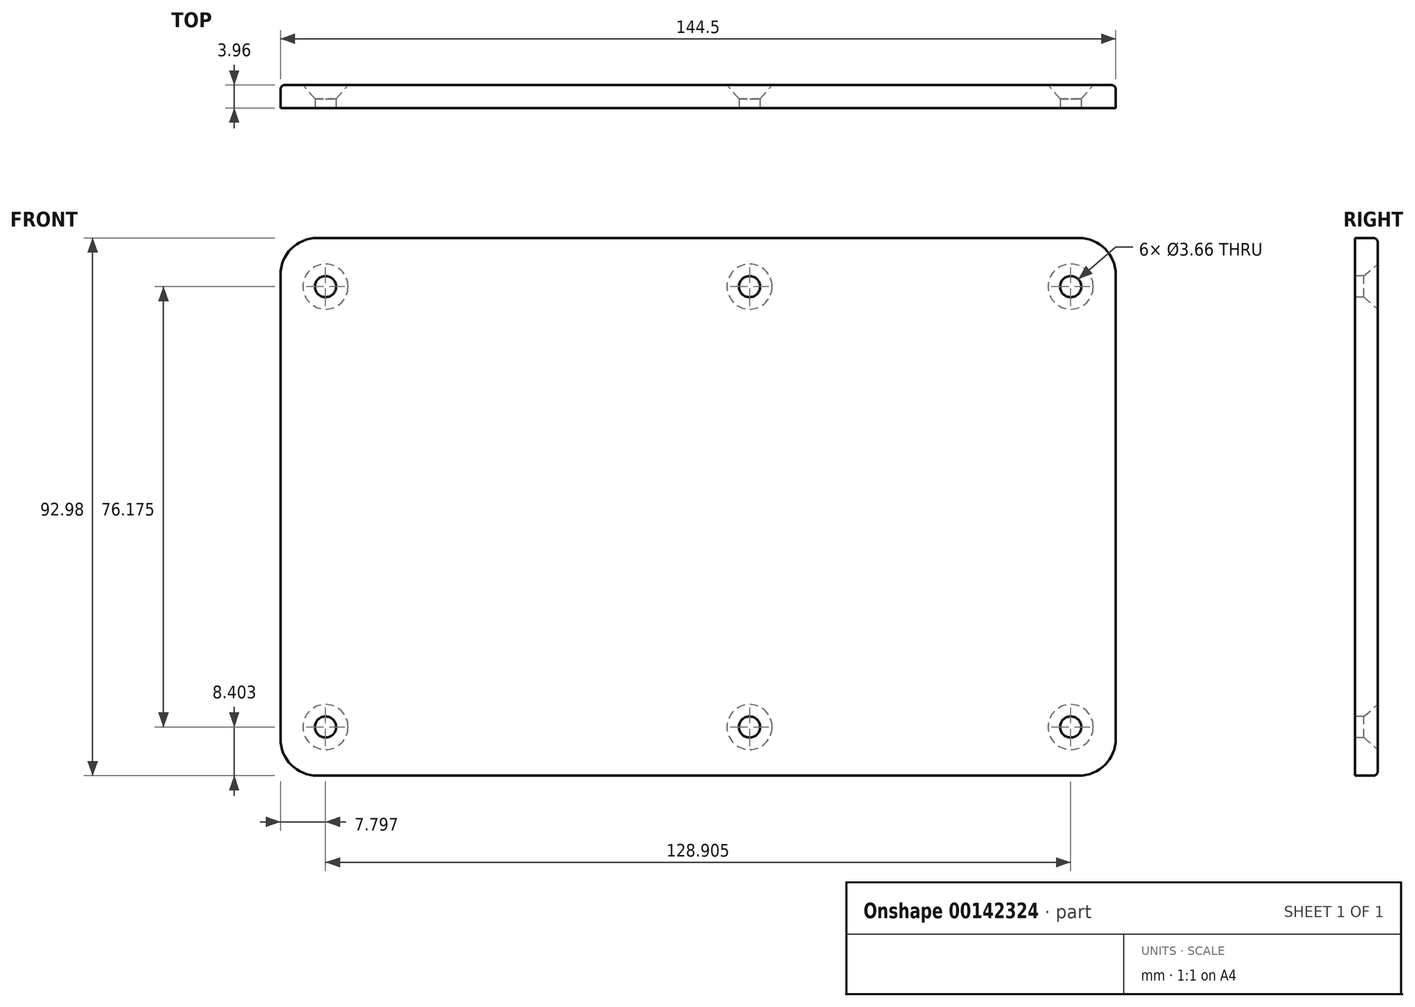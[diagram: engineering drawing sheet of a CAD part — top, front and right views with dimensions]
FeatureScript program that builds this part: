
annotation { "Feature Type Name" : "Feature", "Feature Type Description" : "" }
export const myFeature = defineFeature(function(context is Context, id is Id, definition is map)
    precondition{}
    {
        {
            var Q0;
            Q0=qCreatedBy(makeId("Front.planeOp"),FACE);
            var sketch = newSketch(context, id + "F0", { "sketchPlane" : qUnion([Q0])});
            skLineSegment(sketch, "E0.bottom", {"start": v(-72.25, -46.5) * mm, "end": v(72.25, -46.5) * mm});
            skLineSegment(sketch, "E0.top", {"start": v(-72.25, 46.5) * mm, "end": v(72.25, 46.5) * mm});
            skLineSegment(sketch, "E0.left", {"start": v(-72.25, -46.5) * mm, "end": v(-72.25, 46.5) * mm});
            skLineSegment(sketch, "E0.right", {"start": v(72.25, -46.5) * mm, "end": v(72.25, 46.5) * mm});
            skPoint(sketch, "E0.middle", {"position": v(0, 0) * mm});
            skSolve(sketch);
        }
        {
            var Q0;
            Q0 = qSketchRegion(id + "F0", true);
            extrude(context, id + "F1", {"entities" : qUnion([Q0]), "oppositeDirection" : true, "depth" : 3.96 * mm});
        }
        {
            var Q0;
            Q0=makeQuery(id+"F1.opExtrude","CAP_FACE",FACE,{"disambiguationData":[OSD([sQuery(id+"F0.wireOp",EDGE,"E0.bottom"),sQuery(id+"F0.wireOp",EDGE,"E0.top"),sQuery(id+"F0.wireOp",EDGE,"E0.left"),sQuery(id+"F0.wireOp",EDGE,"E0.right")])],"isStart":false});
            var sketch = newSketch(context, id + "F2", { "sketchPlane" : qUnion([Q0])});
            skPoint(sketch, "E1", {"position": v(-64.45, 38.09) * mm});
            skPoint(sketch, "E2", {"position": v(-64.45, -38.09) * mm});
            skPoint(sketch, "E3", {"position": v(-8.9, 38.09) * mm});
            skPoint(sketch, "E4", {"position": v(64.45, 38.09) * mm});
            skPoint(sketch, "E5", {"position": v(64.45, -38.09) * mm});
            skPoint(sketch, "E6", {"position": v(-8.9, -38.09) * mm});
            skSolve(sketch);
        }
        {
            var Q0;
            Q0=sQuery(id+"F2.wireOp",VERTEX,"E1");
            var Q1;
            Q1=sQuery(id+"F2.wireOp",VERTEX,"E3");
            var Q2;
            Q2=sQuery(id+"F2.wireOp",VERTEX,"E4");
            var Q3;
            Q3=sQuery(id+"F2.wireOp",VERTEX,"E5");
            var Q4;
            Q4=sQuery(id+"F2.wireOp",VERTEX,"E6");
            var Q5;
            Q5=sQuery(id+"F2.wireOp",VERTEX,"E2");
            var Q6;
            Q6=makeQuery(id+"F1.opExtrude","SWEPT_BODY",BODY,{"disambiguationData":[OSD([sQuery(id+"F0.wireOp",EDGE,"E0.bottom"),sQuery(id+"F0.wireOp",EDGE,"E0.top"),sQuery(id+"F0.wireOp",EDGE,"E0.left"),sQuery(id+"F0.wireOp",EDGE,"E0.right")])]});
            hole(context, id + "F3", {"style" : HoleStyle.C_SINK, "endStyle" : HoleEndStyle.THROUGH, "standardTappedOrClearance" : lookupTablePath({ "standard" : "ANSI", "fit" : "Close", "size" : "#6", "type" : "Clearance" }), "standardBlindInLast" : lookupTablePath({ "fit" : "Close", "standard" : "ANSI", "size" : "#6", "type" : "Clearance" }), "holeDiameter" : 3.66 * mm, "cSinkDiameter" : 7.8 * mm, "cSinkAngle" : 82 * degree, "locations" : qUnion([Q0, Q1, Q2, Q3, Q4, Q5]), "scope" : qUnion([Q6]), "isTappedThrough" : true, "startStyle" : HoleStartStyle.SKETCH});
        }
        {
            var Q0;
            Q0=makeQuery(id+"F1.opExtrude","SWEPT_EDGE",EDGE,{"disambiguationData":[OSD([sQuery(id+"F0.wireOp",EDGE,"E0.top"),sQuery(id+"F0.wireOp",EDGE,"E0.right")])]});
            var Q1;
            Q1=makeQuery(id+"F1.opExtrude","SWEPT_EDGE",EDGE,{"disambiguationData":[OSD([sQuery(id+"F0.wireOp",EDGE,"E0.bottom"),sQuery(id+"F0.wireOp",EDGE,"E0.right")])]});
            var Q2;
            Q2=makeQuery(id+"F1.opExtrude","SWEPT_EDGE",EDGE,{"disambiguationData":[OSD([sQuery(id+"F0.wireOp",EDGE,"E0.bottom"),sQuery(id+"F0.wireOp",EDGE,"E0.left")])]});
            var Q3;
            Q3=makeQuery(id+"F1.opExtrude","SWEPT_EDGE",EDGE,{"disambiguationData":[OSD([sQuery(id+"F0.wireOp",EDGE,"E0.top"),sQuery(id+"F0.wireOp",EDGE,"E0.left")])]});
            fillet(context, id + "F4", {"entities" : qUnion([Q0, Q1, Q2, Q3]), "radius" : 6.35 * mm, "tangentPropagation" : true, "allowEdgeOverflow" : false});
        }
        {
            var Q0;
            Q0=makeQuery(id+"F1.opExtrude","CAP_EDGE",EDGE,{"disambiguationData":[OSD([sQuery(id+"F0.wireOp",EDGE,"E0.bottom")])],"isStart":false});
            fillet(context, id + "F5", {"entities" : qUnion([Q0]), "radius" : 0.76 * mm, "tangentPropagation" : true, "allowEdgeOverflow" : false});
        }
    });
